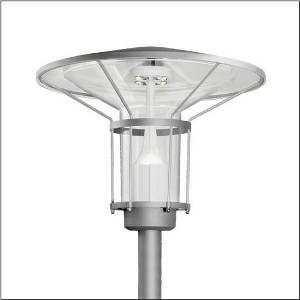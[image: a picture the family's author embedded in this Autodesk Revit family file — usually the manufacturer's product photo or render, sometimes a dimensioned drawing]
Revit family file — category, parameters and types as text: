
# Revit family: laterne_classic_iq___p1_0a_5xa5245nf14h_cdb6
name_source: partatom
category: Lighting Fixtures
units: mm (PartAtom-declared; Revit-internal decimal feet)

## family parameters
Cut with Voids When Loaded = No
Host = Face
Light Source = No
Part Type = Normal
Room Calculation Point = No
Round Connector Dimension = Use Diameter
Shared = No

## types (1)
- --- (1 x LED, 1360 lm, 11.8 W, 2700K)
    Apparent Load = 12 VA
    CIE Flux Codes = 30 61 91 96 100
    Color Rendering = 70
    Color Temperature = 2700K
    Default Elevation = 1800 mm
    Description = Lantern Classic iQ, mast luminaire, Module 540 iQ-SR, primary light control with 3 zone facetted reflector, of plastic, silver coated, highly specular, structured, primary optical cover: cover, of PMMA, transparent, light distribution: P1.0a, light emission: direct distribution, primary light characteristic: strongly asymmetric, installation type: post-top, LED, High Power LED, rated luminous flux: 1.360lm, luminous efficacy: 115lm/W, light colour: 727, colour temperature: 2700K, control gear: ECG iQ, control: presetting dimming logarithmic, Street-Remote, Auto-Match, Temp-Guard, Lumen-Switch, Night-Set, Smart-Wire, Light-Fading, Desk-Remote (wireless, voltage-free reading and setting of iQ features in the workshop via application-optimized NFC function/RFID function), optimised constant luminous flux control (CLO 2.0), with terminal, 6-pole, max. 2.5mm², mains connection: 220..240V, AC, 50/60Hz, start of lifetime: 12W, end of lifetime: 12W, reduction: 5W, luminaire housing, upper part, of glass-fibre reinforced polyester, coated, Siteco® metallic grey (DB 702S), diameter: 750mm, height: 596mm, spigot size: d x l = 76 x 70mm (post-top) | with reducer (optional accessory) 60 x 70mm, post-top mast mounting element, of diecast aluminium, coated, Siteco® metallic grey (DB 702S), Module 540 iQ-SR, traffic white (RAL 9016), equipment: standard, protection rating (complete): IP65, insulation class (complete): insulation class II (safety insulation), certification: CE, ENEC, VDE, packaging unit: 1 piece

Light Distribution: P1.0a
    Height = 596 mm
    Lamp = 1 x LED
    Lamp Light Flux = 1360 lm
    Lamp Power = 11.8 W
    Lamp count = 1
    Length = 750 mm
    Luminous efficacy = 115 lm/W
    Manufacturer = Siteco
    ModVariant = No
    Model = 5XA5245NF14H
    Number of Poles = 1
    OnlyDefault = Yes
    Power Factor = 1
    Product Name = Laterne Classic iQ | P1.0a
    Product group = mast luminaire | pylon top
    ProductGroupID = 6100
    Protection Class = Protection class II
    Protection Degree = IP 65
    RLX_Detail_Level = 1
    RlxData = <blob elided: 94121 chars, md5=a8dce9a6>
    Socket = socket
    Standby Power = 0 W
    System Light Flux = 1360 lm
    System Power = 12 W
    Type Comments = factory setting: luminous flux: 100 % | dim-lin: 254 | 472 mA
    Type Image = l_1006052.jpg
    URL = http://relux.com
    VarID = @adj_063153
    Voltage = 0 V
    Weight = 0.00 kg
    Width = 0 mm  [stored 0 ft]

note: [stored X ft] marks values corroborated as IEEE doubles in the binary element streams (Revit-internal decimal feet)

## geometry (parser evidence)
native form markers: Blend x4, Sweep x12
no freeform markers — native parametric forms only
